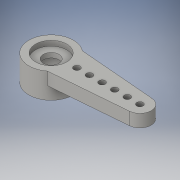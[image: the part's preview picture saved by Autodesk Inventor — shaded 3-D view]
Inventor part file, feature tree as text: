
AUTODESK INVENTOR PART (.ipt)
format: ipt  version: 2016 (Build 200138000, 138)  size: 161,280 bytes
history: native  units: in
note: dims shown in document units (in); Inventor stores cm internally (conversion verified against a paired STEP export)
features: other x3, sketch x1
ambient origin geometry x8: Origin, YZ Plane, XZ Plane, XY Plane, X Axis, Y Axis, Z Axis, Center Point
bodies: Solid1 (feature_tree)
feature tree (4):
  other  "SG90 plastic Horn.ipt"
  other  "Solid1::SG90 plastic Horn.ipt"
  other  "TaggingFeature1"
  sketch  "Sketch1"  dims[d0=0.3937in]
